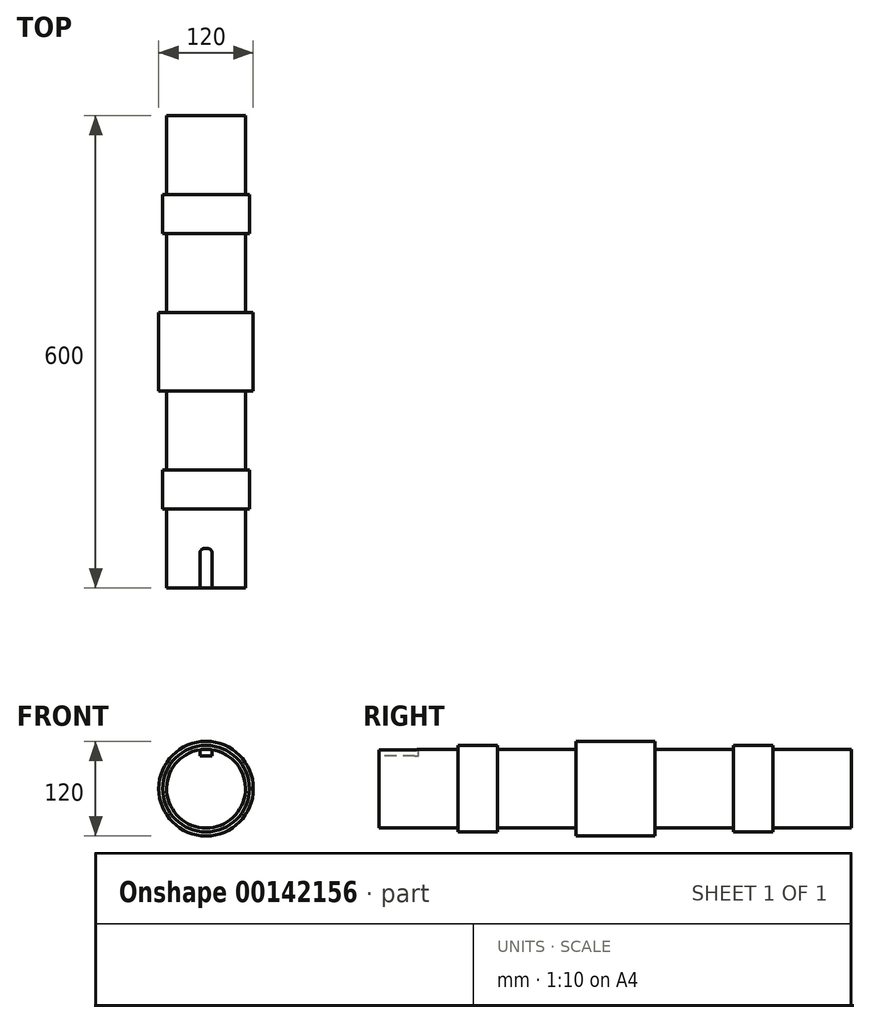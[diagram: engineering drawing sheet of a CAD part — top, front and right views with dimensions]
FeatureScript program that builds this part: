
annotation { "Feature Type Name" : "Feature", "Feature Type Description" : "" }
export const myFeature = defineFeature(function(context is Context, id is Id, definition is map)
    precondition{}
    {
        {
            var Q0;
            Q0=qCreatedBy(makeId("Right.planeOp"),FACE);
            var sketch = newSketch(context, id + "F0", { "sketchPlane" : qUnion([Q0])});
            skLineSegment(sketch, "E0", {"start": v(146.49, 0) * mm, "end": v(-147.7, 0) * mm, "construction": true});
            skLineSegment(sketch, "E1", {"start": v(-300, 0) * mm, "end": v(-300, 50) * mm});
            skLineSegment(sketch, "E2", {"start": v(-300, 50) * mm, "end": v(-200, 50) * mm});
            skLineSegment(sketch, "E3", {"start": v(-200, 50) * mm, "end": v(-200, 55) * mm});
            skLineSegment(sketch, "E4", {"start": v(-200, 55) * mm, "end": v(-150, 55) * mm});
            skLineSegment(sketch, "E5", {"start": v(-150, 55) * mm, "end": v(-150, 50) * mm});
            skLineSegment(sketch, "E6", {"start": v(-150, 50) * mm, "end": v(-50, 50) * mm});
            skLineSegment(sketch, "E7", {"start": v(-50, 50) * mm, "end": v(-50, 60) * mm});
            skLineSegment(sketch, "E8", {"start": v(-50, 60) * mm, "end": v(50, 60) * mm});
            skLineSegment(sketch, "E9", {"start": v(50, 60) * mm, "end": v(50, 50) * mm});
            skLineSegment(sketch, "E10", {"start": v(50, 50) * mm, "end": v(150, 50) * mm});
            skLineSegment(sketch, "E11", {"start": v(150, 50) * mm, "end": v(150, 55) * mm});
            skLineSegment(sketch, "E12", {"start": v(150, 55) * mm, "end": v(200, 55) * mm});
            skLineSegment(sketch, "E13", {"start": v(200, 55) * mm, "end": v(200, 50) * mm});
            skLineSegment(sketch, "E14", {"start": v(200, 50) * mm, "end": v(300, 50) * mm});
            skLineSegment(sketch, "E15", {"start": v(300, 50) * mm, "end": v(300, 0) * mm});
            skLineSegment(sketch, "E16", {"start": v(0, 0) * mm, "end": v(0, -47.35) * mm, "construction": true});
            skLineSegment(sketch, "E17", {"start": v(-300, 0) * mm, "end": v(300, 0) * mm});
            skSolve(sketch);
        }
        {
            var Q0;
            Q0=makeQuery(id+"F0.imprint","IMPRINT",FACE,{"disambiguationData":[TD([[makeQuery(id+"F0.imprint","IMPRINT",EDGE,{"derivedFrom":sQuery(id+"F0.wireOp",EDGE,"E1")}),-1.0]])]});
            var Q1;
            Q1=sQuery(id+"F0.wireOp",EDGE,"E17");
            revolve(context, id + "F1", {"entities" : qUnion([Q0]), "axis" : qUnion([Q1]), "revolveType" : RevolveType.FULL});
        }
        {
            var Q0;
            Q0=makeQuery(id+"F1.opRevolve","SWEPT_FACE",FACE,{"disambiguationData":[OSD([sQuery(id+"F0.wireOp",EDGE,"E1")])]});
            var sketch = newSketch(context, id + "F2", { "sketchPlane" : qUnion([Q0])});
            skLineSegment(sketch, "E18.bottom", {"start": v(7.5, 41.43) * mm, "end": v(-7.5, 41.43) * mm});
            skLineSegment(sketch, "E18.left", {"start": v(7.5, 41.43) * mm, "end": v(7.5, 49.43) * mm});
            skLineSegment(sketch, "E18.right", {"start": v(-7.5, 41.43) * mm, "end": v(-7.5, 49.43) * mm});
            skPoint(sketch, "E18.middle", {"position": v(0, 50) * mm});
            skArc(sketch, "E19.0", {"start": v(7.5, 49.43) * mm, "mid": v(0, 50) * mm, "end": v(-7.5, 49.43) * mm});
            skSolve(sketch);
        }
        {
            var Q0;
            Q0 = qSketchRegion(id + "F2", true);
            extrude(context, id + "F3", {"entities" : qUnion([Q0]), "operationType" : NewBodyOperationType.REMOVE, "oppositeDirection" : true, "depth" : 50 * mm});
        }
        {
            var Q0;
            Q0=makeQuery(id+"F3.boolean.opBoolean","COPY",EDGE,{"derivedFrom":makeQuery(id+"F3.opExtrude","CAP_EDGE",EDGE,{"disambiguationData":[OSD([sQuery(id+"F2.wireOp",EDGE,"E18.right")])],"isStart":false})});
            var Q1;
            Q1=makeQuery(id+"F3.boolean.opBoolean","COPY",EDGE,{"derivedFrom":makeQuery(id+"F3.opExtrude","CAP_EDGE",EDGE,{"disambiguationData":[OSD([sQuery(id+"F2.wireOp",EDGE,"E18.left")])],"isStart":false})});
            fillet(context, id + "F4", {"entities" : qUnion([Q0, Q1]), "radius" : 5 * mm, "tangentPropagation" : true, "allowEdgeOverflow" : false});
        }
    });
